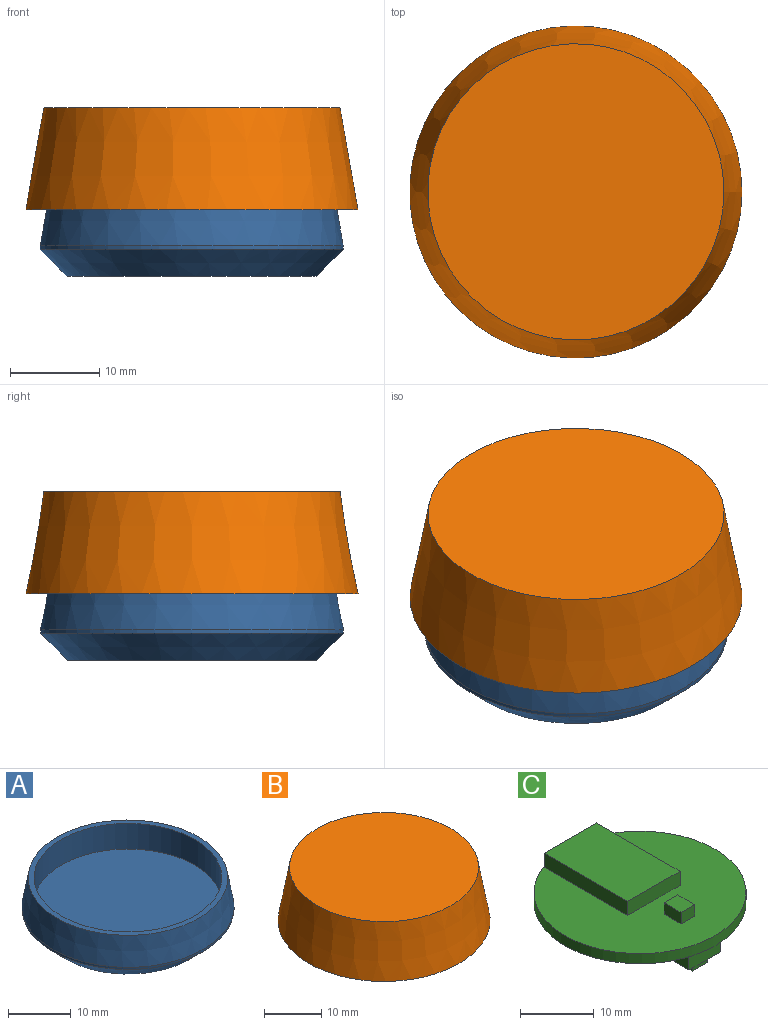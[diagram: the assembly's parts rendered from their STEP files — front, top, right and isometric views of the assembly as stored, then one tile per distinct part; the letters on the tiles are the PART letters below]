
ASSEMBLY  parts=3 mates=2
PART A: 7 faces, bbox 33.9x33.9x9 mm
  f0: cylinder r=16.94mm len=33.87mm, axis (0,0,1), area 45.1mm2, adj f2,f3
  f1: plane 27.87x27.87mm, normal (0,0,-1), area 610.1mm2, adj f2
  f2: cone r=16.94mm half-angle=45deg, axis (0,0,1), area 411.5mm2, adj f0,f1
  f3: cone r=14.88mm half-angle=10deg, axis (0,0,-1), area 585mm2, adj f0,f6
  f4: plane 30x30mm, normal (0,0,1), area 706.9mm2, adj f5
  f5: cylinder r=15mm len=30mm, axis (0,0,-1), area 471.2mm2, adj f4,f6
  f6: plane 31.9x31.9mm, normal (0,0,1), area 92.6mm2, adj f3,f5
PART B: 38 faces, bbox 37.1x37.1x11.4 mm
  f0: plane 4.69x1.85mm, normal (0.38,-0.92,0), area 6.8mm2, adj f2,f3,f4,f5,f6,f7,f8,f9
  f1: plane 4.69x1.85mm, normal (0.38,0.92,0), area 6.8mm2, adj f2,f3,f4,f5,f6,f7,f8,f9
  f2: cylinder r=13.35mm len=10.22mm, axis (0,0,-1), area 18.1mm2, adj f0,f1,f6,f9
  f3: cylinder r=15.35mm len=11.75mm, axis (0,0,-1), area 46.8mm2, adj f0,f1,f5,f10
  f4: cone r=13.35mm half-angle=45deg, axis (0,0,-1), area 20.1mm2, adj f0,f1,f5,f8
  f5: plane 11.75x1.82mm, normal (0,0,-1), area 8.3mm2, adj f0,f1,f3,f4
  f6: plane 10.98x2.02mm, normal (0,0,-1), area 10.9mm2, adj f0,f1,f2,f7
  f7: cylinder r=14.35mm len=10.98mm, axis (0,0,-1), area 18.8mm2, adj f0,f1,f6,f8
  f8: plane 10.98x2.02mm, normal (0,0,1), area 10.9mm2, adj f0,f1,f4,f7
  f9: plane 29.9x28.1mm, normal (0,0,-1), area 502.5mm2, adj f0,f1,f2,f10,f11,f12,f13,f16
  f10: cone r=14.97mm half-angle=10deg, axis (0,0,-1), area 978.6mm2, adj f0,f1,f3,f9,f11,f13,f14,f17
  f11: plane 1.93x1.73mm, normal (0.97,0.26,0), area 3.4mm2, adj f9,f10,f12,f14,f15
  f12: cylinder r=13.35mm len=6.91mm, axis (0,0,-1), area 12.1mm2, adj f9,f11,f13,f15
  f13: plane 1.93x1.73mm, normal (-0.97,0.26,0), area 3.4mm2, adj f9,f10,f12,f14,f15
  f14: cylinder r=15.35mm len=7.95mm, axis (0,0,-1), area 7.4mm2, adj f10,f11,f13,f15
  f15: plane 7.95x2.46mm, normal (0,0,-1), area 15mm2, adj f11,f12,f13,f14
  f16: cylinder r=13.35mm len=10.22mm, axis (0,0,-1), area 18.1mm2, adj f9,f17,f18,f22
  f17: plane 4.69x1.85mm, normal (-0.38,0.92,0), area 6.8mm2, adj f9,f10,f16,f19,f20,f21,f22,f23
  f18: plane 4.69x1.85mm, normal (-0.38,-0.92,0), area 6.8mm2, adj f9,f10,f16,f19,f20,f21,f22,f23
  f19: cylinder r=15.35mm len=11.75mm, axis (0,0,-1), area 46.8mm2, adj f10,f17,f18,f21
  f20: cone r=13.35mm half-angle=45deg, axis (0,0,-1), area 20.1mm2, adj f17,f18,f21,f24
  f21: plane 11.75x1.82mm, normal (0,0,-1), area 8.3mm2, adj f17,f18,f19,f20
  f22: plane 10.98x2.02mm, normal (0,0,-1), area 10.9mm2, adj f16,f17,f18,f23
  f23: cylinder r=14.35mm len=10.98mm, axis (0,0,-1), area 18.8mm2, adj f17,f18,f22,f24
  f24: plane 10.98x2.02mm, normal (0,0,1), area 10.9mm2, adj f17,f18,f20,f23
  f25: cone r=16.55mm half-angle=10deg, axis (0,0,-1), area 1276.8mm2, adj f26,f27
  f26: plane 33.1x33.1mm, normal (0,0,1), area 860.5mm2, adj f25
  f27: plane 37.12x37.12mm, normal (0,0,-1), area 181.2mm2, adj f10,f25
  f28: plane 16x10mm, normal (0,0,-1), area 160mm2, adj f29,f30,f31,f32
  f29: plane 16x0.6mm, normal (-1,0,0), area 9.6mm2, adj f9,f28,f30,f32
  f30: plane 10x0.6mm, normal (0,1,0), area 6mm2, adj f9,f28,f29,f31
  f31: plane 16x0.6mm, normal (1,0,0), area 9.6mm2, adj f9,f28,f30,f32
  f32: plane 10x0.6mm, normal (0,-1,0), area 6mm2, adj f9,f28,f29,f31
  f33: plane 2.6x0.17mm, normal (0,-1,0), area 0.4mm2, adj f9,f34,f36,f37
  f34: plane 3.25x0.17mm, normal (1,0,0), area 0.6mm2, adj f9,f33,f35,f37
  f35: plane 2.6x0.17mm, normal (0,1,0), area 0.4mm2, adj f9,f34,f36,f37
  f36: plane 3.25x0.17mm, normal (-1,0,0), area 0.6mm2, adj f9,f33,f35,f37
  f37: plane 3.25x2.6mm, normal (0,0,-1), area 8.4mm2, adj f33,f34,f35,f36
PART C: 23 faces, bbox 28.7x28.7x8.9 mm
  f0: plane 6x3.2mm, normal (0,0,-1), area 15.1mm2, adj f9,f10,f11,f12,f13,f14,f15,f16
  f1: plane 28.7x28.7mm, normal (0,0,-1), area 627.7mm2, adj f3,f9,f10,f11,f12
  f2: plane 28.7x28.7mm, normal (0,0,1), area 478.5mm2, adj f3,f4,f5,f6,f7,f18,f19,f20
  f3: cylinder r=14.35mm len=28.7mm, axis (0,0,-1), area 150.6mm2, adj f1,f2
  f4: plane 2.6x1.9mm, normal (0,1,0), area 4.9mm2, adj f2,f5,f7,f8
  f5: plane 3.25x1.9mm, normal (-1,0,0), area 6.2mm2, adj f2,f4,f6,f8
  f6: plane 2.6x1.9mm, normal (0,-1,0), area 4.9mm2, adj f2,f5,f7,f8
  f7: plane 3.25x1.9mm, normal (1,0,0), area 6.2mm2, adj f2,f4,f6,f8
  f8: plane 3.25x2.6mm, normal (0,0,1), area 8.4mm2, adj f4,f5,f6,f7
  f9: plane 3.5x3.2mm, normal (1,0,0), area 11.2mm2, adj f0,f1,f10,f12
  f10: plane 6x3.5mm, normal (0,1,0), area 21mm2, adj f0,f1,f9,f11
  f11: plane 3.5x3.2mm, normal (-1,0,0), area 11.2mm2, adj f0,f1,f10,f12
  f12: plane 6x3.5mm, normal (0,-1,0), area 21mm2, adj f0,f1,f9,f11
  f13: plane 1.4x1.4mm, normal (-1,0,0), area 2mm2, adj f0,f14,f16,f17
  f14: plane 2.9x1.4mm, normal (0,-1,0), area 4.1mm2, adj f0,f13,f15,f17
  f15: plane 1.4x1.4mm, normal (1,0,0), area 2mm2, adj f0,f14,f16,f17
  f16: plane 2.9x1.4mm, normal (0,1,0), area 4.1mm2, adj f0,f13,f15,f17
  f17: plane 2.9x1.4mm, normal (0,0,-1), area 4.1mm2, adj f13,f14,f15,f16
  f18: plane 10x2.33mm, normal (0,1,0), area 23.3mm2, adj f2,f19,f21,f22
  f19: plane 16x2.33mm, normal (-1,0,0), area 37.3mm2, adj f2,f18,f20,f22
  f20: plane 10x2.33mm, normal (0,-1,0), area 23.3mm2, adj f2,f19,f21,f22
  f21: plane 16x2.33mm, normal (1,0,0), area 37.3mm2, adj f2,f18,f20,f22
  f22: plane 16x10mm, normal (0,0,1), area 160mm2, adj f18,f19,f20,f21
PLACE A t=(-0.68,2.89,-34.06)mm
PLACE B t=(-0.68,2.89,-30.64)mm
PLACE C t=(-0.68,2.89,-30.64)mm
MATE fastened C.f8 <-> B.f37  axis (0,0,-1) through (-0.68,-1.98,-27.07)mm
MATE slider B.f12 <-> A.f5  axis (0,0,1) through (-0.68,5.54,-27.24)mm
